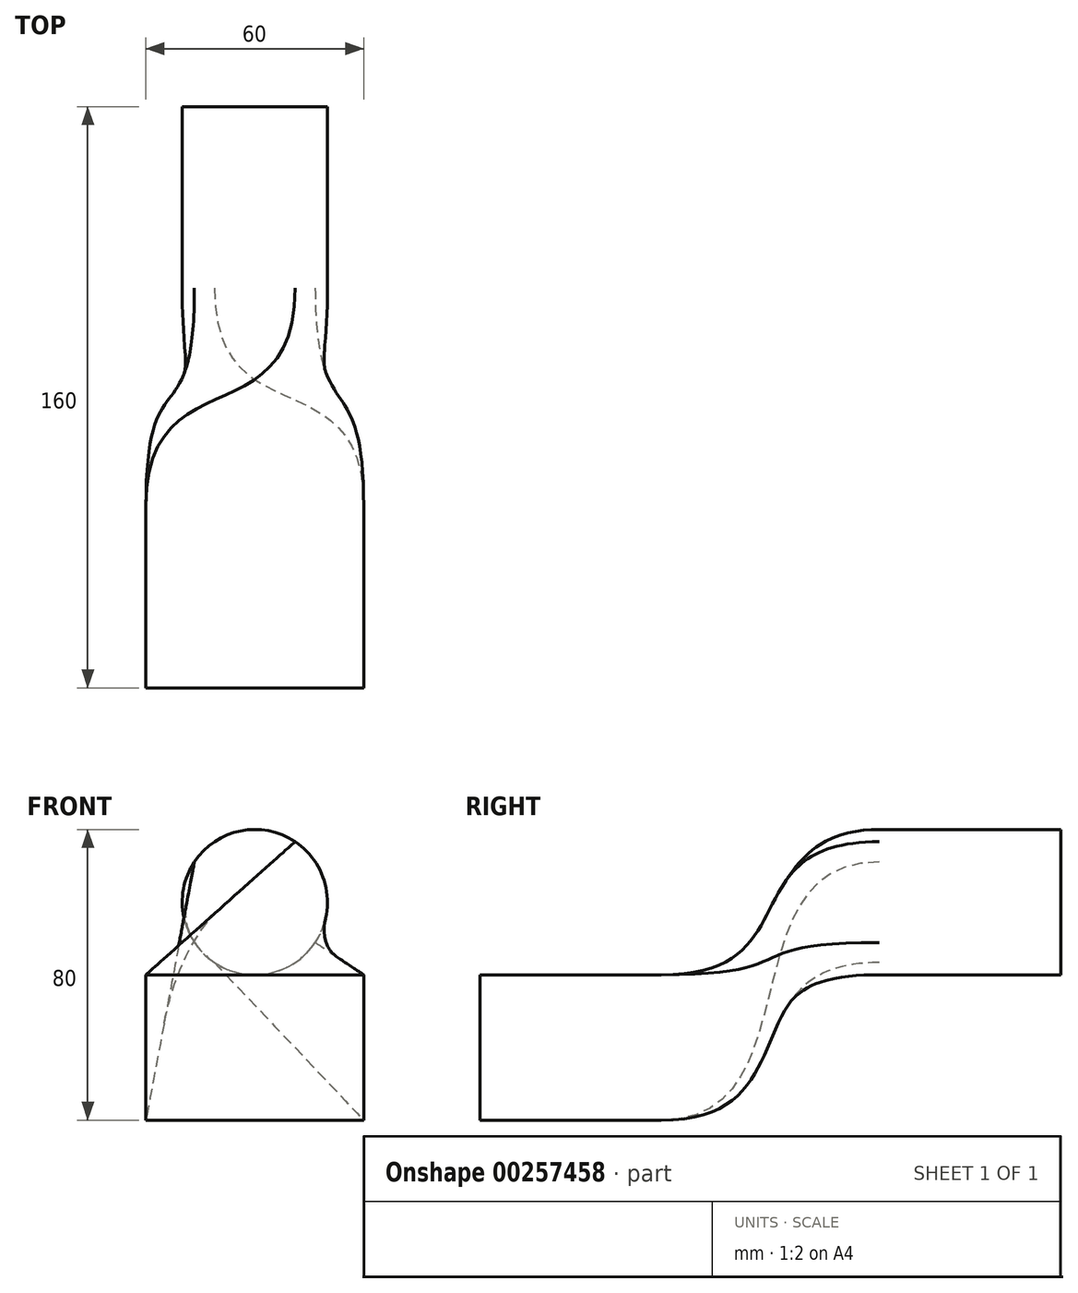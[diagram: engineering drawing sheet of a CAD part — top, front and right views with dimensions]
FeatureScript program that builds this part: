
annotation { "Feature Type Name" : "Feature", "Feature Type Description" : "" }
export const myFeature = defineFeature(function(context is Context, id is Id, definition is map)
    precondition{}
    {
        {
            var Q0;
            Q0=qCreatedBy(makeId("Front.planeOp"),FACE);
            cPlane(context, id + "F0", {"entities" : qUnion([Q0]), "cplaneType" : CPlaneType.OFFSET, "offset" : 160 * mm, "width" : 150 * mm, "height" : 150 * mm});
        }
        {
            var Q0;
            Q0=qCreatedBy(id+"F0.planeOp",FACE);
            var sketch = newSketch(context, id + "F1", { "sketchPlane" : qUnion([Q0])});
            skLineSegment(sketch, "E0.bottom", {"start": v(30, 20) * mm, "end": v(-30, 20) * mm});
            skLineSegment(sketch, "E0.top", {"start": v(30, -20) * mm, "end": v(-30, -20) * mm});
            skLineSegment(sketch, "E0.left", {"start": v(30, 20) * mm, "end": v(30, -20) * mm});
            skLineSegment(sketch, "E0.right", {"start": v(-30, 20) * mm, "end": v(-30, -20) * mm});
            skPoint(sketch, "E0.middle", {"position": v(0, 0) * mm});
            skSolve(sketch);
        }
        {
            var Q0;
            Q0=qCreatedBy(makeId("Front.planeOp"),FACE);
            var sketch = newSketch(context, id + "F2", { "sketchPlane" : qUnion([Q0])});
            skCircle(sketch, "E1", {"center": v(0, 40) * mm, "radius": 20 * mm});
            skLineSegment(sketch, "E2.0", {"start": v(30, 20) * mm, "end": v(-30, 20) * mm, "construction": true});
            skSolve(sketch);
        }
        {
            var Q0;
            Q0=makeQuery(id+"F1.imprint","IMPRINT",FACE,{"disambiguationData":[TD([[makeQuery(id+"F1.imprint","IMPRINT",EDGE,{"derivedFrom":sQuery(id+"F1.wireOp",EDGE,"E0.bottom")}),1.0]])]});
            extrude(context, id + "F3", {"entities" : qUnion([Q0]), "oppositeDirection" : true, "depth" : 50 * mm});
        }
        {
            var Q0;
            Q0=makeQuery(id+"F2.imprint","IMPRINT",FACE,{"disambiguationData":[TD([[makeQuery(id+"F2.imprint","IMPRINT",EDGE,{"derivedFrom":sQuery(id+"F2.wireOp",EDGE,"E1")}),1.0]])]});
            extrude(context, id + "F4", {"entities" : qUnion([Q0]), "depth" : 50 * mm});
        }
        {
            var Q1;
            Q1=makeQuery(id+"F4.opExtrude","CAP_FACE",FACE,{"disambiguationData":[OSD([sQuery(id+"F2.wireOp",EDGE,"E1")])],"isStart":false});
            var Q2;
            Q2=makeQuery(id+"F3.opExtrude","CAP_FACE",FACE,{"disambiguationData":[OSD([sQuery(id+"F1.wireOp",EDGE,"E0.bottom"),sQuery(id+"F1.wireOp",EDGE,"E0.top"),sQuery(id+"F1.wireOp",EDGE,"E0.left"),sQuery(id+"F1.wireOp",EDGE,"E0.right")])],"isStart":false});
            loft(context, id + "F5", {"operationType" : NewBodyOperationType.ADD, "startCondition" : LoftEndDerivativeType.MATCH_TANGENT, "startMagnitude" : 2, "endCondition" : LoftEndDerivativeType.MATCH_TANGENT, "endMagnitude" : 2, "sheetProfilesArray" : [{ "sheetProfileEntities" : qUnion([Q1]) }, { "sheetProfileEntities" : qUnion([Q2]) }]});
        }
    });
